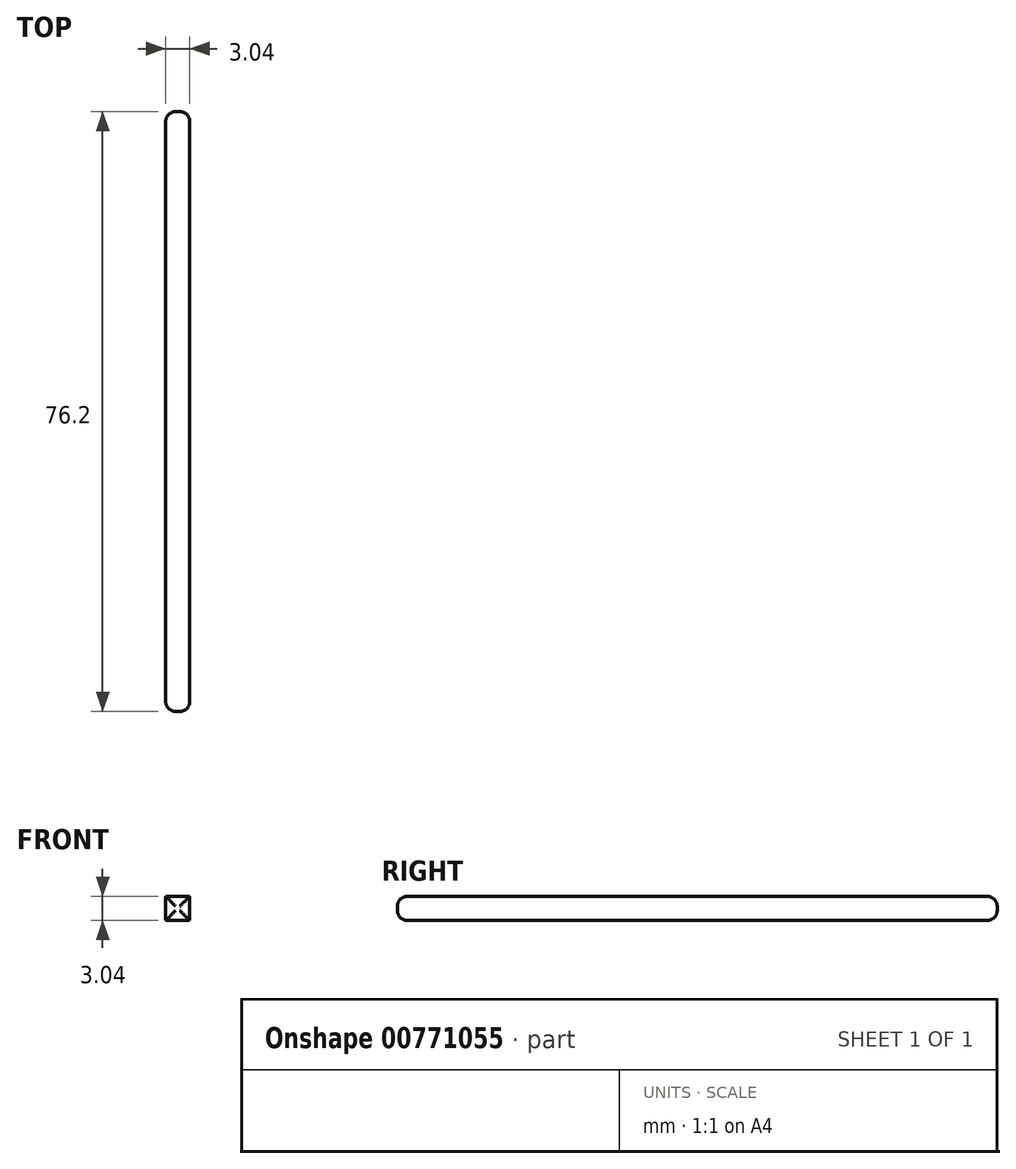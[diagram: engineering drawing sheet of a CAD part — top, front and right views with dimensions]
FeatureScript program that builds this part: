
annotation { "Feature Type Name" : "Feature", "Feature Type Description" : "" }
export const myFeature = defineFeature(function(context is Context, id is Id, definition is map)
    precondition{}
    {
        {
            var Q0;
            Q0=qCreatedBy(makeId("Front.planeOp"),FACE);
            var sketch = newSketch(context, id + "F0", { "sketchPlane" : qUnion([Q0])});
            skLineSegment(sketch, "E0.bottom", {"start": v(1.52, -1.52) * mm, "end": v(-1.52, -1.52) * mm});
            skLineSegment(sketch, "E0.top", {"start": v(1.52, 1.52) * mm, "end": v(-1.52, 1.52) * mm});
            skLineSegment(sketch, "E0.left", {"start": v(1.52, -1.52) * mm, "end": v(1.52, 1.52) * mm});
            skLineSegment(sketch, "E0.right", {"start": v(-1.52, -1.52) * mm, "end": v(-1.52, 1.52) * mm});
            skPoint(sketch, "E0.middle", {"position": v(0, 0) * mm});
            skSolve(sketch);
        }
        {
            var Q0;
            Q0=makeQuery(id+"F0.imprint","IMPRINT",FACE,{"disambiguationData":[TD([[makeQuery(id+"F0.imprint","IMPRINT",EDGE,{"derivedFrom":sQuery(id+"F0.wireOp",EDGE,"E0.bottom")}),-1.0]])]});
            extrude(context, id + "F1", {"entities" : qUnion([Q0]), "depth" : 76.2 * mm, "offsetDistance" : 25.4 * mm});
        }
        {
            var Q0;
            Q0=makeQuery(id+"F1.opExtrude","CAP_EDGE",EDGE,{"disambiguationData":[OSD([sQuery(id+"F0.wireOp",EDGE,"E0.top")])],"isStart":false});
            var Q1;
            Q1=makeQuery(id+"F1.opExtrude","CAP_EDGE",EDGE,{"disambiguationData":[OSD([sQuery(id+"F0.wireOp",EDGE,"E0.left")])],"isStart":false});
            var Q2;
            Q2=makeQuery(id+"F1.opExtrude","CAP_EDGE",EDGE,{"disambiguationData":[OSD([sQuery(id+"F0.wireOp",EDGE,"E0.right")])],"isStart":false});
            var Q3;
            Q3=makeQuery(id+"F1.opExtrude","CAP_EDGE",EDGE,{"disambiguationData":[OSD([sQuery(id+"F0.wireOp",EDGE,"E0.bottom")])],"isStart":false});
            var Q4;
            Q4=makeQuery(id+"F1.opExtrude","CAP_EDGE",EDGE,{"disambiguationData":[OSD([sQuery(id+"F0.wireOp",EDGE,"E0.left")])],"isStart":true});
            var Q5;
            Q5=makeQuery(id+"F1.opExtrude","CAP_EDGE",EDGE,{"disambiguationData":[OSD([sQuery(id+"F0.wireOp",EDGE,"E0.bottom")])],"isStart":true});
            var Q6;
            Q6=makeQuery(id+"F1.opExtrude","CAP_EDGE",EDGE,{"disambiguationData":[OSD([sQuery(id+"F0.wireOp",EDGE,"E0.top")])],"isStart":true});
            var Q7;
            Q7=makeQuery(id+"F1.opExtrude","CAP_EDGE",EDGE,{"disambiguationData":[OSD([sQuery(id+"F0.wireOp",EDGE,"E0.right")])],"isStart":true});
            fillet(context, id + "F2", {"entities" : qUnion([Q0, Q1, Q2, Q3, Q4, Q5, Q6, Q7]), "radius" : 1.27 * mm, "tangentPropagation" : true, "allowEdgeOverflow" : false});
        }
    });
